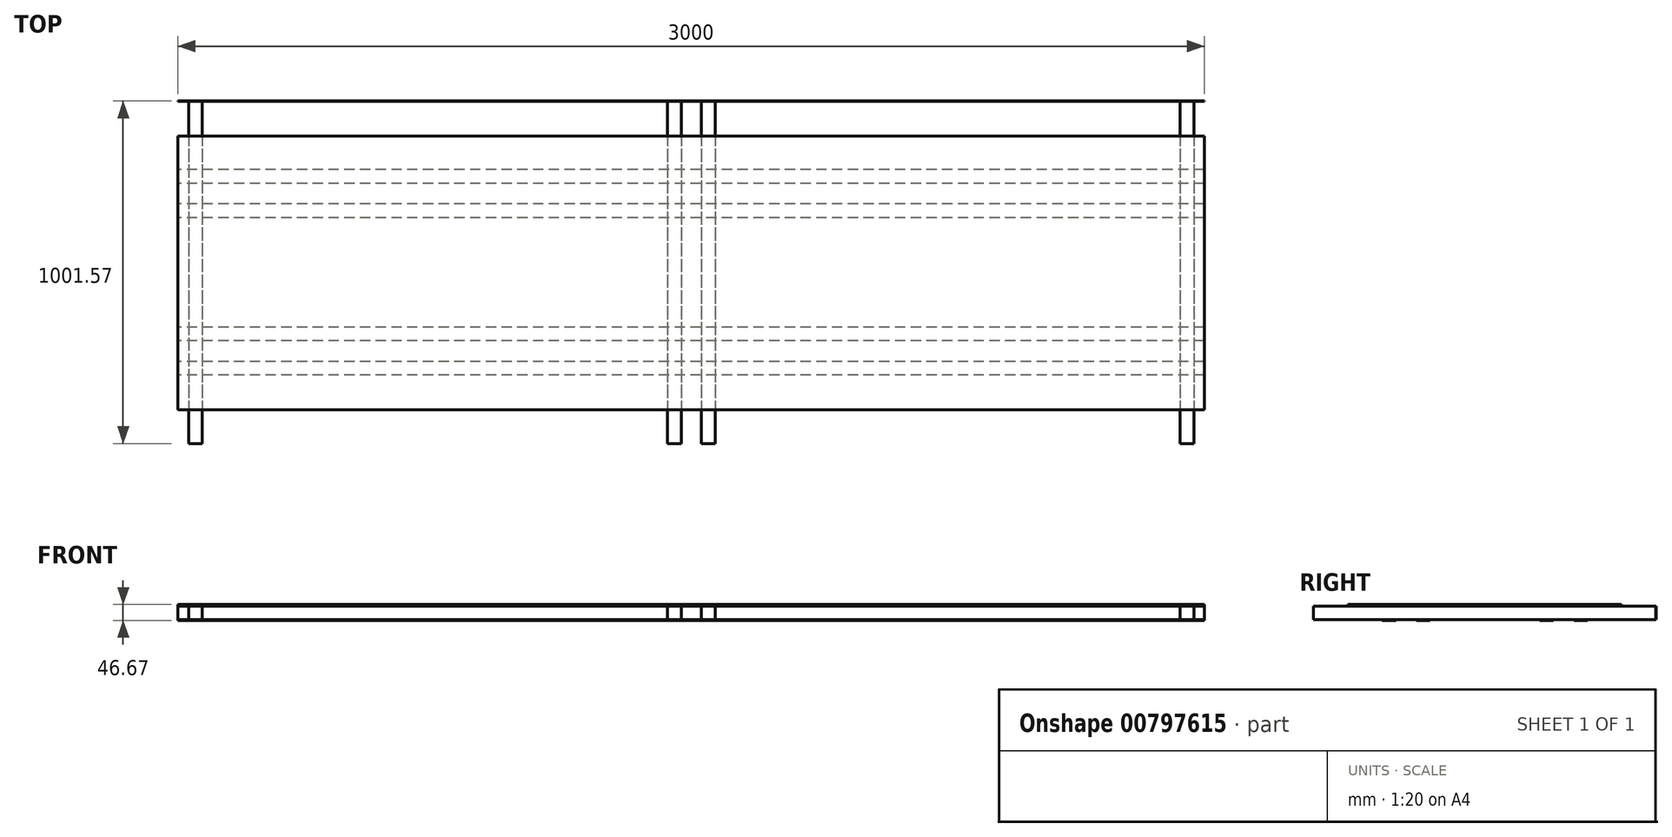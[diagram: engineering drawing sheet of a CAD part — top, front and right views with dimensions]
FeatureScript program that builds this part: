
annotation { "Feature Type Name" : "Feature", "Feature Type Description" : "" }
export const myFeature = defineFeature(function(context is Context, id is Id, definition is map)
    precondition{}
    {
        {
            var Q0;
            Q0=qCreatedBy(makeId("Front.planeOp"),FACE);
            var sketch = newSketch(context, id + "F0", { "sketchPlane" : qUnion([Q0])});
            skLineSegment(sketch, "E0.bottom", {"start": v(30.85, 0) * mm, "end": v(70.85, 0) * mm});
            skLineSegment(sketch, "E0.top", {"start": v(30.85, 40) * mm, "end": v(70.85, 40) * mm});
            skLineSegment(sketch, "E0.left", {"start": v(30.85, 0) * mm, "end": v(30.85, 40) * mm});
            skLineSegment(sketch, "E0.right", {"start": v(70.85, 0) * mm, "end": v(70.85, 40) * mm});
            skLineSegment(sketch, "E1.bottom", {"start": v(1431.28, 0) * mm, "end": v(1471.28, 0) * mm});
            skLineSegment(sketch, "E1.top", {"start": v(1431.28, 40) * mm, "end": v(1471.28, 40) * mm});
            skLineSegment(sketch, "E1.left", {"start": v(1431.28, 0) * mm, "end": v(1431.28, 40) * mm});
            skLineSegment(sketch, "E1.right", {"start": v(1471.28, 0) * mm, "end": v(1471.28, 40) * mm});
            skLineSegment(sketch, "E2.bottom", {"start": v(1530.51, 0) * mm, "end": v(1570.51, 0) * mm});
            skLineSegment(sketch, "E2.top", {"start": v(1530.51, 40) * mm, "end": v(1570.51, 40) * mm});
            skLineSegment(sketch, "E2.left", {"start": v(1530.51, 0) * mm, "end": v(1530.51, 40) * mm});
            skLineSegment(sketch, "E2.right", {"start": v(1570.51, 0) * mm, "end": v(1570.51, 40) * mm});
            skLineSegment(sketch, "E3.bottom", {"start": v(2930.2, 0) * mm, "end": v(2970.2, 0) * mm});
            skLineSegment(sketch, "E3.top", {"start": v(2930.2, 40) * mm, "end": v(2970.2, 40) * mm});
            skLineSegment(sketch, "E3.left", {"start": v(2930.2, 0) * mm, "end": v(2930.2, 40) * mm});
            skLineSegment(sketch, "E3.right", {"start": v(2970.2, 0) * mm, "end": v(2970.2, 40) * mm});
            skSolve(sketch);
        }
        {
            var Q0;
            Q0 = qSketchRegion(id + "F0", true);
            extrude(context, id + "F1", {"entities" : qUnion([Q0]), "oppositeDirection" : true, "depth" : 1000 * mm, "offsetDistance" : 25.4 * mm});
        }
        {
            var Q0;
            Q0=qCreatedBy(makeId("Right.planeOp"),FACE);
            var sketch = newSketch(context, id + "F2", { "sketchPlane" : qUnion([Q0])});
            skLineSegment(sketch, "E4.bottom", {"start": v(800.92, 0) * mm, "end": v(760.92, 0) * mm});
            skLineSegment(sketch, "E4.top", {"start": v(800.92, -1.5) * mm, "end": v(760.92, -1.5) * mm});
            skLineSegment(sketch, "E4.left", {"start": v(800.92, 0) * mm, "end": v(800.92, -1.5) * mm});
            skLineSegment(sketch, "E4.right", {"start": v(760.92, 0) * mm, "end": v(760.92, -1.5) * mm});
            skLineSegment(sketch, "E5.bottom", {"start": v(700.62, 0) * mm, "end": v(660.62, 0) * mm});
            skLineSegment(sketch, "E5.top", {"start": v(700.62, -1.5) * mm, "end": v(660.62, -1.5) * mm});
            skLineSegment(sketch, "E5.left", {"start": v(700.62, 0) * mm, "end": v(700.62, -1.5) * mm});
            skLineSegment(sketch, "E5.right", {"start": v(660.62, 0) * mm, "end": v(660.62, -1.5) * mm});
            skLineSegment(sketch, "E6.bottom", {"start": v(340.24, 0) * mm, "end": v(300.24, 0) * mm});
            skLineSegment(sketch, "E6.top", {"start": v(340.24, -1.5) * mm, "end": v(300.24, -1.5) * mm});
            skLineSegment(sketch, "E6.left", {"start": v(340.24, 0) * mm, "end": v(340.24, -1.5) * mm});
            skLineSegment(sketch, "E6.right", {"start": v(300.24, 0) * mm, "end": v(300.24, -1.5) * mm});
            skLineSegment(sketch, "E7.bottom", {"start": v(200.31, 0) * mm, "end": v(240.31, 0) * mm});
            skLineSegment(sketch, "E7.top", {"start": v(200.31, -1.5) * mm, "end": v(240.31, -1.5) * mm});
            skLineSegment(sketch, "E7.left", {"start": v(200.31, 0) * mm, "end": v(200.31, -1.5) * mm});
            skLineSegment(sketch, "E7.right", {"start": v(240.31, 0) * mm, "end": v(240.31, -1.5) * mm});
            skSolve(sketch);
        }
        {
            var Q0;
            Q0 = qSketchRegion(id + "F2", true);
            extrude(context, id + "F3", {"entities" : qUnion([Q0]), "depth" : 3000 * mm, "offsetDistance" : 25.4 * mm});
        }
        {
            var Q0;
            Q0=qCreatedBy(makeId("Right.planeOp"),FACE);
            var sketch = newSketch(context, id + "F4", { "sketchPlane" : qUnion([Q0])});
            skLineSegment(sketch, "E8.bottom", {"start": v(1001.57, 0) * mm, "end": v(1000.07, 0) * mm});
            skLineSegment(sketch, "E8.top", {"start": v(1001.57, 40) * mm, "end": v(1000.07, 40) * mm});
            skLineSegment(sketch, "E8.left", {"start": v(1001.57, 0) * mm, "end": v(1001.57, 40) * mm});
            skLineSegment(sketch, "E8.right", {"start": v(1000.07, 0) * mm, "end": v(1000.07, 40) * mm});
            skSolve(sketch);
        }
        {
            var Q0;
            Q0 = qSketchRegion(id + "F4", true);
            extrude(context, id + "F5", {"entities" : qUnion([Q0]), "depth" : 3000 * mm, "offsetDistance" : 25.4 * mm});
        }
        {
            var Q0;
            Q0=qCreatedBy(makeId("Right.planeOp"),FACE);
            var sketch = newSketch(context, id + "F6", { "sketchPlane" : qUnion([Q0])});
            skLineSegment(sketch, "E9.bottom", {"start": v(99.3, 40.17) * mm, "end": v(899.3, 40.17) * mm});
            skLineSegment(sketch, "E9.top", {"start": v(99.3, 45.17) * mm, "end": v(899.3, 45.17) * mm});
            skLineSegment(sketch, "E9.left", {"start": v(99.3, 40.17) * mm, "end": v(99.3, 45.17) * mm});
            skLineSegment(sketch, "E9.right", {"start": v(899.3, 40.17) * mm, "end": v(899.3, 45.17) * mm});
            skSolve(sketch);
        }
        {
            var Q0;
            Q0 = qSketchRegion(id + "F6", true);
            extrude(context, id + "F7", {"entities" : qUnion([Q0]), "depth" : 3000 * mm, "offsetDistance" : 25.4 * mm});
        }
    });
